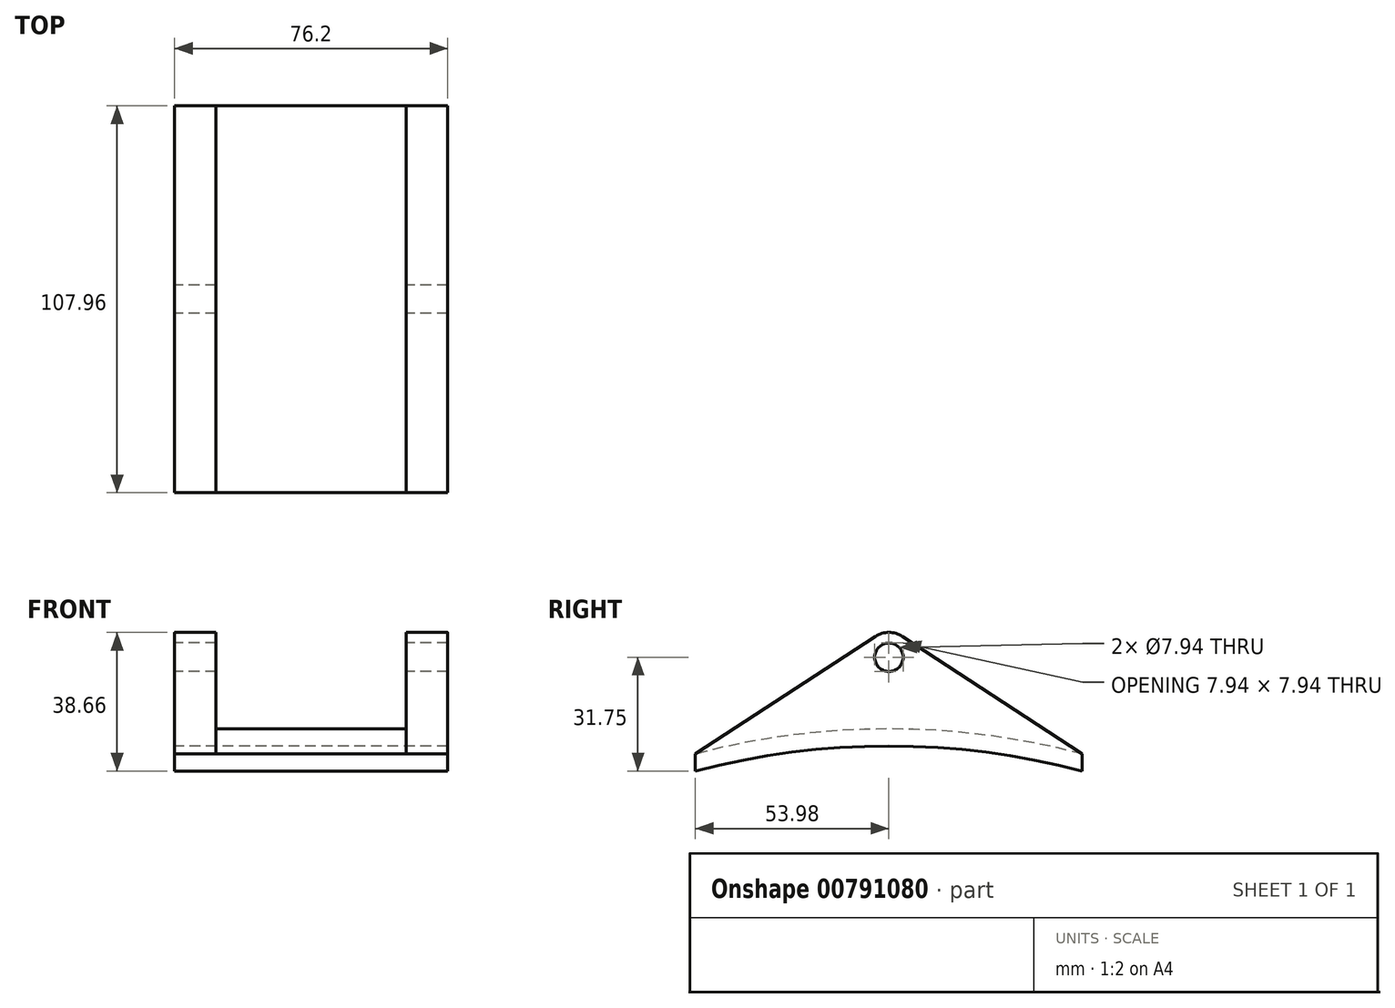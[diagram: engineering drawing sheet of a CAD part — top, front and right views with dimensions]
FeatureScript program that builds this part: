
annotation { "Feature Type Name" : "Feature", "Feature Type Description" : "" }
export const myFeature = defineFeature(function(context is Context, id is Id, definition is map)
    precondition{}
    {
        {
            var Q0;
            Q0=qCreatedBy(makeId("Right.planeOp"),FACE);
            var sketch = newSketch(context, id + "F0", { "sketchPlane" : qUnion([Q0])});
            skLineSegment(sketch, "E0", {"start": v(-53.97, 0) * mm, "end": v(-53.97, 4.76) * mm});
            skLineSegment(sketch, "E1", {"start": v(-53.98, 4.76) * mm, "end": v(-3.78, 37.54) * mm});
            skLineSegment(sketch, "E2", {"start": v(3.78, 37.54) * mm, "end": v(53.98, 4.76) * mm});
            skLineSegment(sketch, "E3", {"start": v(53.98, 4.76) * mm, "end": v(53.98, 0) * mm});
            skPoint(sketch, "E4.visualSharp", {"position": v(0, 40) * mm});
            skArc(sketch, "E4.filletArc", {"start": v(3.78, 37.54) * mm, "mid": v(0, 38.66) * mm, "end": v(-3.78, 37.54) * mm});
            skCircle(sketch, "E5", {"center": v(0, 31.75) * mm, "radius": 3.97 * mm});
            skPoint(sketch, "E6", {"position": v(0, 6.99) * mm});
            skArc(sketch, "E7", {"start": v(53.98, 0) * mm, "mid": v(0, 6.98) * mm, "end": v(-53.97, 0) * mm});
            skSolve(sketch);
        }
        {
            var Q0;
            Q0 = qSketchRegion(id + "F0", true);
            extrude(context, id + "F1", {"entities" : qUnion([Q0]), "depth" : 76.2 * mm, "offsetDistance" : 25.4 * mm});
        }
        {
            var Q0;
            Q0=makeQuery(id+"F1.opExtrude","CAP_FACE",FACE,{"disambiguationData":[OSD([sQuery(id+"F0.wireOp",EDGE,"E0"),sQuery(id+"F0.wireOp",EDGE,"E1"),sQuery(id+"F0.wireOp",EDGE,"E2"),sQuery(id+"F0.wireOp",EDGE,"E3"),sQuery(id+"F0.wireOp",EDGE,"E4.filletArc"),sQuery(id+"F0.wireOp",EDGE,"E5"),sQuery(id+"F0.wireOp",EDGE,"E7")])],"isStart":true});
            cPlane(context, id + "F2", {"entities" : qUnion([Q0]), "cplaneType" : CPlaneType.OFFSET, "offset" : 38.1 * mm, "oppositeDirection" : true, "width" : 152.4 * mm, "height" : 152.4 * mm});
        }
        {
            var Q0;
            Q0=qCreatedBy(id+"F2.planeOp",FACE);
            var sketch = newSketch(context, id + "F3", { "sketchPlane" : qUnion([Q0])});
            skLineSegment(sketch, "E8.0", {"start": v(-3.78, 37.54) * mm, "end": v(-53.98, 4.76) * mm});
            skArc(sketch, "E9.0", {"start": v(-3.78, 37.54) * mm, "mid": v(0, 38.66) * mm, "end": v(3.78, 37.54) * mm});
            skLineSegment(sketch, "E10.0", {"start": v(53.98, 4.76) * mm, "end": v(3.78, 37.54) * mm});
            skArc(sketch, "E11", {"start": v(53.97, 4.76) * mm, "mid": v(0, 11.75) * mm, "end": v(-53.97, 4.76) * mm});
            skSolve(sketch);
        }
        {
            var Q0;
            Q0 = qSketchRegion(id + "F3", true);
            extrude(context, id + "F4", {"entities" : qUnion([Q0]), "operationType" : NewBodyOperationType.REMOVE, "depth" : 26.54 * mm, "offsetDistance" : 25.4 * mm, "hasSecondDirection" : true, "secondDirectionOppositeDirection" : true, "secondDirectionDepth" : 26.54 * mm});
        }
    });
